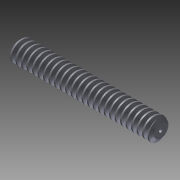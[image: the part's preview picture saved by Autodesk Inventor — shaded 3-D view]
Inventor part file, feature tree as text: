
AUTODESK INVENTOR PART (.ipt)
format: ipt  version: 2011 (Build 150239000, 239)  size: 669,184 bytes
history: native  units: mm (DEFAULTED — no unit token found)
features: other x6, chamfer x2, pattern_circular x2, extrude x1, hole x1, sketch x1
ambient origin geometry x6: Origin, XZ Plane, X Axis, Y Axis, Z Axis, Center Point
bodies: Solid1 (feature_tree)
feature tree (13):
  extrude  "Base Body"  Depth=4.026691mm
  chamfer  "Chamfer1"  Distance=85.0mm
  chamfer  "Chamfer2"  [1 undecoded]
  other  "Tooth Sketch"
  other  "Tooth"
  pattern_circular  "Tooth Pattern"  [2 undecoded]
  other  "Left Tooth"
  pattern_circular  "Left Tooth Pattern"  [2 undecoded]
  hole  "Hole1"  [1 undecoded]
  other  "Base Body Sketch"
  sketch  "Sketch5"  dims[d4=40.0mm d5=4.026691mm d6=85.0mm d7=0.0mm d8=0.268693mm d9=0.738227mm d10=0.268693mm d11=0.738227mm d12=19.198622mm d14=3.1425mm d24=19.198622mm d25=43.748682mm d26=0.263546mm d27=1.275119mm d28=1.677788mm d29=2.033479mm d30=1.054185mm d31=10.0mm d32=830.0mm d33=0.0mm d34=90.0deg d35=90.0deg d36=0.0mm d37=0.0mm d44=10.0mm d46=360.0deg d47=45.0deg d48=45.0deg d49=3.355575mm d50=0.0mm d54=0.0mm d56=0.0mm d59=3.355575mm d60=10.0mm d61=0.0mm d62=1.054185mm d63=10.0mm d64=830.0mm d65=0.0mm d66=90.0deg d67=90.0deg d68=0.0mm d69=0.0mm d70=10.0mm d71=10.0mm d72=10.0mm d73=360.0deg d75=10.0mm d76=10.0mm d77=0.0mm d79=3.355575mm d80=0.0mm d81=10.0mm d82=10.0mm d83=2.0mm d84=6.0mm d85=4.0mm d86=2.0mm d87=90.0deg d88=8.0mm d89=20.594885mm]
  other  "Srf1"
  other  "Pitch Diameter"
note: 6 required parameter values undecoded (feature->parameter linkage not recoverable at this tier; creation-order binding heuristic only, values carry confidence <= 0.55)
